# Revit family: GRAS_HW-19N-2030 EPM
name_source: partatom
category: Osprzęt hydrauliczny
revit_build: Autodesk Revit 2018 (Build: 20190510_1515(x64)
units: mm (PartAtom-declared; Revit-internal decimal feet)

## family parameters
Obiekt nadrzędny = Powierzchnia
Punkt obliczania pomieszczeń = Nie
Tnij formami wycięć po wczytaniu = Nie
Typ części = Normalny
Współdzielony = Nie
Wymiar okrągłego złącza = Użyj średnicy

## types (2) — shared parameters
Cabinet height = 865 mm  [stored 2.83793 ft]
Cabinet width = 930 mm  [stored 3.05118 ft]
DN = 19 mm  [stored 0.062336 ft]
Flow = 35.0 L/s
H = 100 mm  [stored 0.328084 ft]
K Factor = 42
Producent = GRAS PPPH
URL = https://gras.pl
W = 70 mm  [stored 0.229659 ft]
zero-valued in all types: Domyślna rzędna

## per-type parameters (varying)
| type | Cabinet depth | Cabinet material |
| HW-19N-20/30 EPM, RAL3000 | 170 mm  [stored 0.557743 ft] | DC01, RAL3000 |
| HW-19N-20/30 EPM, RAL9010 | 220 mm  [stored 0.721785 ft] | DC01, RAL9010 |

note: column(s) folded — value = type name in every type: Model

note: [stored X ft] marks values corroborated as IEEE doubles in the binary element streams (Revit-internal decimal feet)

## geometry (parser evidence)
native form markers: Blend x8
no freeform markers — native parametric forms only
